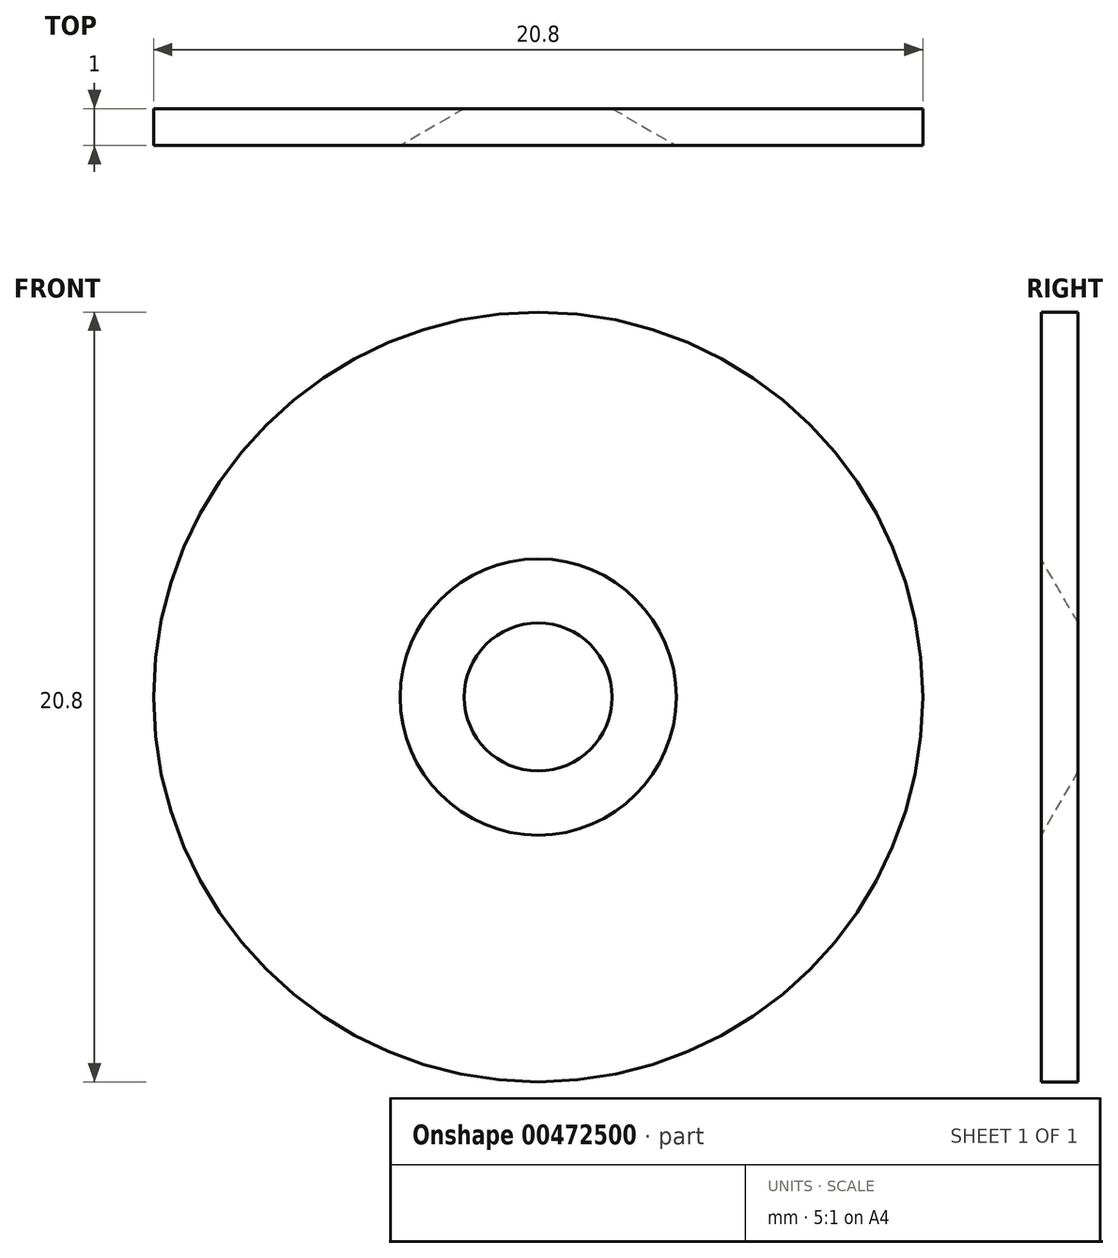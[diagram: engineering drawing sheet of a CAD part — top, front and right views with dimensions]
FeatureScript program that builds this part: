
annotation { "Feature Type Name" : "Feature", "Feature Type Description" : "" }
export const myFeature = defineFeature(function(context is Context, id is Id, definition is map)
    precondition{}
    {
        {
            var Q0;
            Q0=qCreatedBy(makeId("Top.planeOp"),FACE);
            var sketch = newSketch(context, id + "F0", { "sketchPlane" : qUnion([Q0])});
            skLineSegment(sketch, "E0", {"start": v(0, 36.81) * mm, "end": v(0, -37.82) * mm});
            skSolve(sketch);
        }
        {
            var Q0;
            Q0=qCreatedBy(makeId("Top.planeOp"),FACE);
            var sketch = newSketch(context, id + "F1", { "sketchPlane" : qUnion([Q0])});
            skLineSegment(sketch, "E1", {"start": v(2, 2.58) * mm, "end": v(10.4, 2.58) * mm});
            skLineSegment(sketch, "E2", {"start": v(10.4, 2.58) * mm, "end": v(10.4, 1.58) * mm});
            skLineSegment(sketch, "E3", {"start": v(10.4, 1.58) * mm, "end": v(3.73, 1.58) * mm});
            skLineSegment(sketch, "E4", {"start": v(3.73, 1.58) * mm, "end": v(2, 2.58) * mm});
            skSolve(sketch);
        }
        {
            var Q0;
            Q0=makeQuery(id+"F1.imprint","IMPRINT",FACE,{"disambiguationData":[TD([[makeQuery(id+"F1.imprint","IMPRINT",EDGE,{"derivedFrom":sQuery(id+"F1.wireOp",EDGE,"E1")}),-1.0]])]});
            var Q1;
            Q1=sQuery(id+"F0.wireOp",EDGE,"E0");
            revolve(context, id + "F2", {"surfaceOperationType" : NewSurfaceOperationType.NEW, "entities" : qUnion([Q0]), "axis" : qUnion([Q1]), "revolveType" : RevolveType.FULL});
        }
    });
